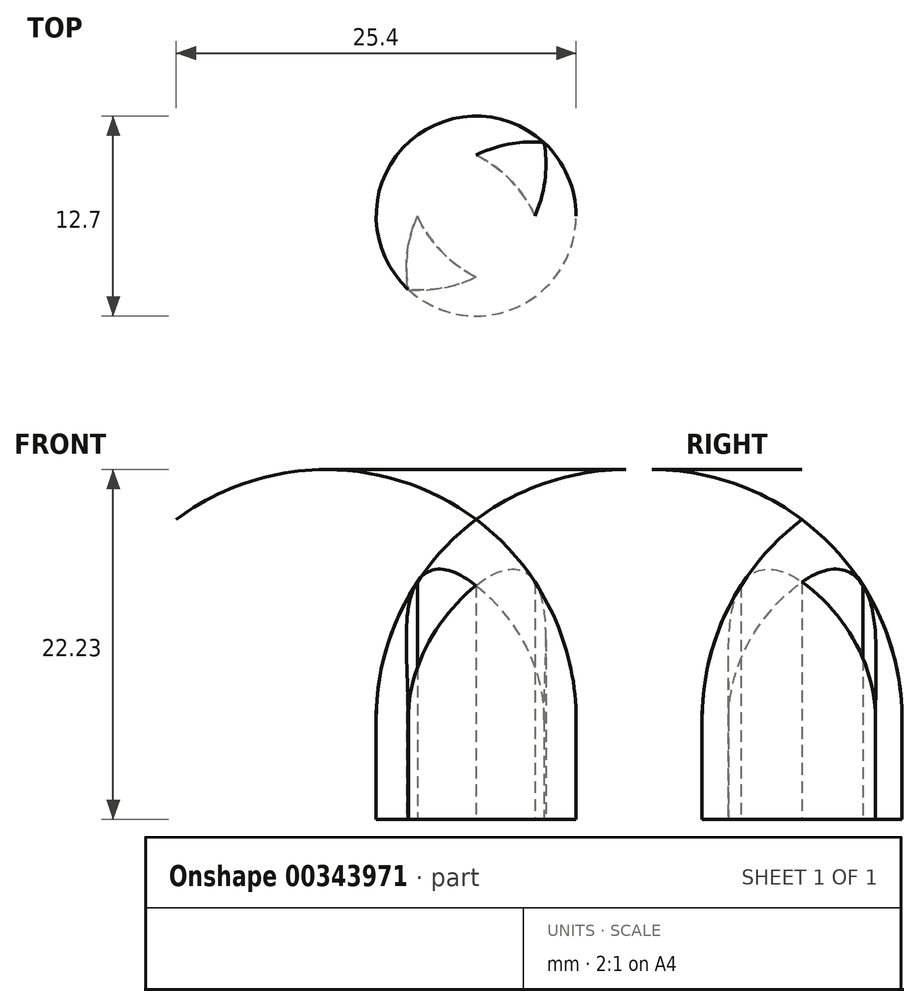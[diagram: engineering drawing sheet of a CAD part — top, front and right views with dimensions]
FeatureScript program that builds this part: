
annotation { "Feature Type Name" : "Feature", "Feature Type Description" : "" }
export const myFeature = defineFeature(function(context is Context, id is Id, definition is map)
    precondition{}
    {
        {
            var Q0;
            Q0=qCreatedBy(makeId("Right.planeOp"),FACE);
            var sketch = newSketch(context, id + "F0", { "sketchPlane" : qUnion([Q0])});
            skLineSegment(sketch, "E0.bottom", {"start": v(0, 0) * mm, "end": v(-6.35, 0) * mm});
            skLineSegment(sketch, "E0.left", {"start": v(0, 0) * mm, "end": v(0, 19.05) * mm});
            skLineSegment(sketch, "E0.right", {"start": v(-6.35, 0) * mm, "end": v(-6.35, 6.35) * mm});
            skPoint(sketch, "E1.visualSharp", {"position": v(-6.35, 23.69) * mm});
            skArc(sketch, "E2", {"start": v(0, 19.05) * mm, "mid": v(-4.67, 13.45) * mm, "end": v(-6.35, 6.35) * mm});
            skSolve(sketch);
        }
        {
            var Q0;
            Q0=makeQuery(id+"F0.imprint","IMPRINT",FACE,{"disambiguationData":[TD([[makeQuery(id+"F0.imprint","IMPRINT",EDGE,{"derivedFrom":sQuery(id+"F0.wireOp",EDGE,"E0.bottom")}),-1.0]])]});
            var Q1;
            Q1=sQuery(id+"F0.wireOp",EDGE,"E0.left");
            revolve(context, id + "F1", {"entities" : qUnion([Q0]), "axis" : qUnion([Q1]), "revolveType" : RevolveType.FULL});
        }
        {
            var Q0;
            Q0=makeQuery(id+"F1.opRevolve","SWEPT_FACE",FACE,{"disambiguationData":[OSD([sQuery(id+"F0.wireOp",EDGE,"E0.bottom")])]});
            var sketch = newSketch(context, id + "F2", { "sketchPlane" : qUnion([Q0])});
            skArc(sketch, "E3", {"start": v(-4.3, -4.67) * mm, "mid": v(2.32, -2.14) * mm, "end": v(4.31, 4.66) * mm});
            skArc(sketch, "E4.MirrorCS", {"start": v(4.3, -4.67) * mm, "mid": v(-2.32, -2.14) * mm, "end": v(-4.31, 4.66) * mm});
            skArc(sketch, "E5.MirrorCS", {"start": v(4.3, 4.67) * mm, "mid": v(-2.32, 2.14) * mm, "end": v(-4.31, -4.66) * mm});
            skArc(sketch, "E6.MirrorCS", {"start": v(-4.3, 4.67) * mm, "mid": v(2.32, 2.14) * mm, "end": v(4.31, -4.66) * mm});
            skSolve(sketch);
        }
        {
            var Q0;
            {var subQ0=sQuery(id+"F2.wireOp",EDGE,"E3");Q0=makeQuery(id+"F2.imprint","IMPRINT",FACE,{"disambiguationData":[TD([[makeQuery(id+"F2.imprint","IMPRINT",EDGE,{"derivedFrom":subQ0}),1.0]])]});}
            var Q1;
            {var subQ0=sQuery(id+"F2.wireOp",EDGE,"E4.MirrorCS");Q1=makeQuery(id+"F2.imprint","IMPRINT",FACE,{"disambiguationData":[TD([[makeQuery(id+"F2.imprint","IMPRINT",EDGE,{"derivedFrom":subQ0}),-1.0]])]});}
            var Q2;
            {var subQ0=sQuery(id+"F2.wireOp",EDGE,"E5.MirrorCS");Q2=makeQuery(id+"F2.imprint","IMPRINT",FACE,{"disambiguationData":[TD([[makeQuery(id+"F2.imprint","IMPRINT",EDGE,{"derivedFrom":subQ0}),1.0]])]});}
            var Q3;
            {var subQ0=sQuery(id+"F2.wireOp",EDGE,"E6.MirrorCS");Q3=makeQuery(id+"F2.imprint","IMPRINT",FACE,{"disambiguationData":[TD([[makeQuery(id+"F2.imprint","IMPRINT",EDGE,{"derivedFrom":subQ0}),-1.0]])]});}
            extrude(context, id + "F3", {"entities" : qUnion([Q0, Q1, Q2, Q3]), "operationType" : NewBodyOperationType.INTERSECT, "endBound" : BoundingType.THROUGH_ALL, "oppositeDirection" : true, "depth" : 25.4 * mm});
        }
    });
